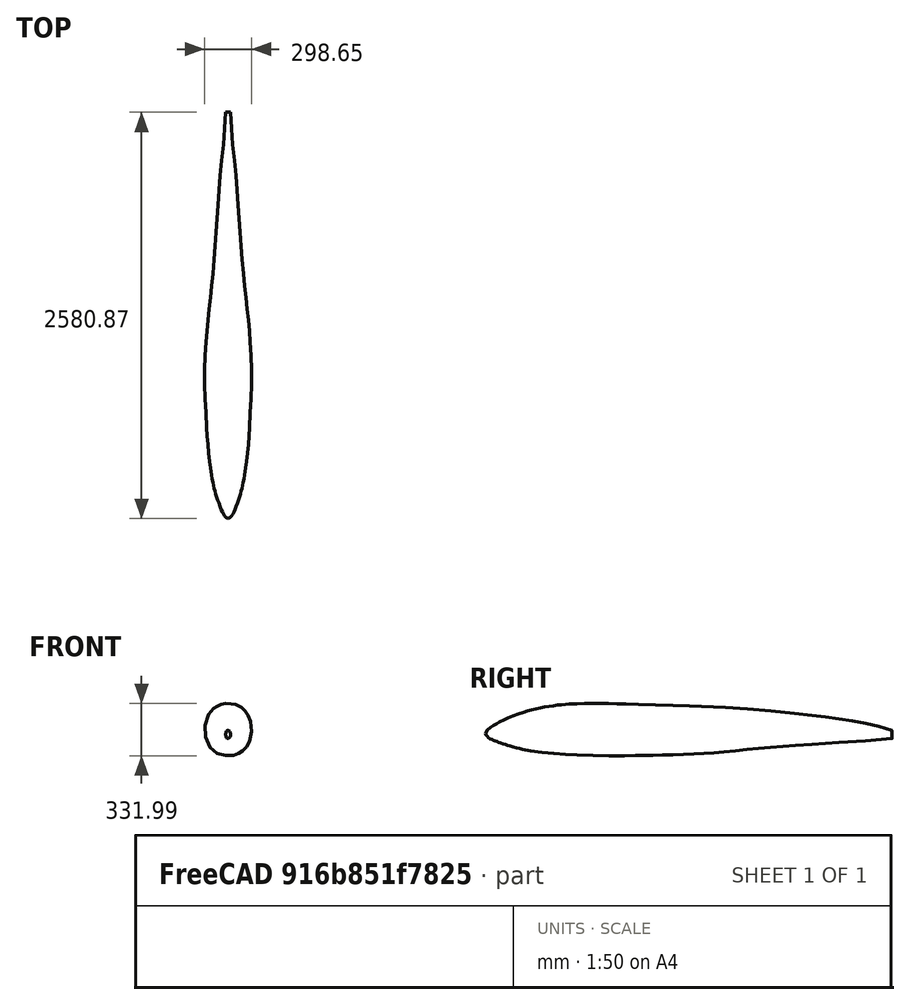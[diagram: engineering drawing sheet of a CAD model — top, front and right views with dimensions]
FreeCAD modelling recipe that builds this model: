
FCSTD DOCUMENT  (FreeCAD 1.0R39319 (Git))
Label: Drone body
License: All rights reserved
LicenseURL: https://en.wikipedia.org/wiki/All_rights_reserved
objects: Image::ImagePlane×3, Sketcher::SketchObject×3, Part::FeaturePython×2, PartDesign::Body×1
note: 9 computed .brp shape members not serialized (recipe doc carries the construction recipe); baked Part::Feature solids carry a one-line shape summary decoded from their .brp

FEATURE [PartDesign::Body] Body
  AllowCompound = false
  Origin = -> Origin
FEATURE [Image::ImagePlane] scheibe_sfh34_3v  label="Top"
  Placement = pos=(96.3,901.7,-4638.1) rot=(0,0,1;0rad)
  XSize = 5853.99
  YSize = 3489.71
FEATURE [Image::ImagePlane] scheibe_sfh34_3v001  label="Front"
  Placement = pos=(84.3,5726.3,1459.8) rot=(1,0,0;1.5708rad)
  XSize = 5853.99
  YSize = 3489.71
FEATURE [Image::ImagePlane] scheibe_sfh34_3v002  label="Right"
  Placement = pos=(-3758.7,-166.6,-638.5) rot=(0.57735,0.57735,0.57735;2.0944rad)
  XSize = 5853.99
  YSize = 3489.71
FEATURE [Sketcher::SketchObject] Sketch  label="HullCurve1"
  ArcFitTolerance = 1e-06
  FullyConstrained = false
  MakeInternals = false
  Placement = pos=(0,0,0) rot=(0.57735,0.57735,0.57735;2.0944rad)
  sketch-geometry (54):
    g0-g10: Circle [constr] x11 (B-spline internal-alignment scaffolding for g11; pole/knot coordinates omitted)
    g11: BSplineCurve PolesCount=11 KnotsCount=9 Degree=3 IsPeriodic=0
    g12-g20: GeomPoint [constr] x9 (B-spline internal-alignment scaffolding for g11; pole/knot coordinates omitted)
    g21-g34: Circle [constr] x14 (B-spline internal-alignment scaffolding for g35; pole/knot coordinates omitted)
    g35: BSplineCurve PolesCount=14 KnotsCount=12 Degree=3 IsPeriodic=0
    g36-g47: GeomPoint [constr] x12 (B-spline internal-alignment scaffolding for g35; pole/knot coordinates omitted)
    g48: Circle [constr] CenterX=2168.64 CenterY=101.192 CenterZ=0 NormalX=0 NormalY=0 NormalZ=1 AngleXU=0 Radius=1
    g49: Circle [constr] CenterX=2352.52 CenterY=83.7723 CenterZ=0 NormalX=0 NormalY=0 NormalZ=1 AngleXU=0 Radius=1
    g50: Circle [constr] CenterX=2583.1 CenterY=17.2095 CenterZ=0 NormalX=0 NormalY=0 NormalZ=1 AngleXU=0 Radius=1
    g51: BSplineCurve PolesCount=3 KnotsCount=2 Degree=2 IsPeriodic=0
    g52: GeomPoint [constr] X=2168.64 Y=101.192 Z=0
    g53: GeomPoint [constr] X=2583.1 Y=17.2095 Z=0
  constraints (22):
    c: Weight(g0) = 1
    c: Equal(g0, g1-g10) x10
    c: InternalAlignment(g0-g10 -> g11) x11
    c: InternalAlignment(g12-g20 -> g11) x9
    c: Coincident(g0,g-1)
    c: PointOnObject(g1,g-2)
    c: Weight(g21) = 1
    c: Equal(g21, g22-g34) x13
    c: InternalAlignment(g21-g34 -> g35) x14
    c: InternalAlignment(g36-g47 -> g35) x12
    c: Coincident(g21,g11)
    c: PointOnObject(g22,g-2)
    c: Weight(g48) = 1
    c: Equal(g48,g49)
    c: Equal(g48,g50)
    c: InternalAlignment(g48,g51)
    c: InternalAlignment(g49,g51)
    c: InternalAlignment(g50,g51)
    c: InternalAlignment(g52,g51)
    c: InternalAlignment(g53,g51)
    c: Coincident(g48,g11)
    c: Vertical(g35,g51)
FEATURE [Sketcher::SketchObject] Sketch001  label="HullCurve2"
  ArcFitTolerance = 1e-06
  FullyConstrained = false
  MakeInternals = false
  sketch-geometry (50):
    g0-g12: Circle [constr] x13 (B-spline internal-alignment scaffolding for g13; pole/knot coordinates omitted)
    g13: BSplineCurve PolesCount=13 KnotsCount=11 Degree=3 IsPeriodic=0
    g14-g24: GeomPoint [constr] x11 (B-spline internal-alignment scaffolding for g13; pole/knot coordinates omitted)
    g25: BSplineCurve PolesCount=13 KnotsCount=11 Degree=3 IsPeriodic=0
    g26-g38: Circle [constr] x13 (B-spline internal-alignment scaffolding for g25; pole/knot coordinates omitted)
    g39-g49: GeomPoint [constr] x11 (B-spline internal-alignment scaffolding for g25; pole/knot coordinates omitted)
  constraints (9):
    c: Weight(g0) = 1
    c: Equal(g0, g1-g12) x12
    c: InternalAlignment(g0-g12 -> g13) x13
    c: InternalAlignment(g14-g24 -> g13) x11
    c: Coincident(g0,g-1)
    c: PointOnObject(g1,g-1)
    c: Weight(g26) = 1
    c: Equal(g26, g27-g38) x12
    c: InternalAlignment(g26-g49 -> g25) x24
FEATURE [Sketcher::SketchObject] Sketch002  label="Profile"
  ArcFitTolerance = 1e-06
  FullyConstrained = true
  MakeInternals = false
  Placement = pos=(0,0,0) rot=(1,0,0;1.5708rad)
  sketch-geometry (10):
    g0-g3: Circle [constr] x4 (B-spline internal-alignment scaffolding for g4; pole/knot coordinates omitted)
    g4: BSplineCurve PolesCount=4 KnotsCount=5 Degree=3 IsPeriodic=1
    g5-g9: GeomPoint [constr] x5 (B-spline internal-alignment scaffolding for g4; pole/knot coordinates omitted)
  constraints (11):
    c: Weight(g0) = 1
    c: Equal(g0,g1)
    c: Equal(g0,g2)
    c: Equal(g0,g3)
    c: InternalAlignment(g0-g3 -> g4) x4
    c: InternalAlignment(g5-g9 -> g4) x5
    c: Symmetric(g0,g1,g-2)
    c: Symmetric(g3,g2,g-2)
    c: DistanceX(g0,g1) = 5
    c: DistanceY(g2,g1) = 5
    c: Symmetric(g2,g1,g-1)
FEATURE [Part::FeaturePython] CurvedArray  label="Body001"  # WARN: FeaturePython — macro-defined, semantics opaque (R4)
  Axis = (0,1,0)
  Base = -> Sketch002
  Distribution = 1
  DistributionReverse = false
  Hullcurves = -> [Sketch001,Sketch]
  Items = 20
  KeepBase = 0
  LoftMaxDegree = 2
  MaxLoftSize = 13
  OffsetEnd = 0
  OffsetStart = 0
  Solid = true
  Surface = false
  Twist = 0
FEATURE [Part::FeaturePython] wrib  # WARN: FeaturePython — macro-defined, semantics opaque (R4)
  Chord = 350
  Coordinates = (401) [(1.00008,0,0.00125721),(1.00002,0,0.00126996),(0.999839,0,0.00130819),(0.999534,0,0.00137188),(0.999106,0,0.00146099),(0.998557,0,0.00157543),+395 more]
  NacaNbrPoint = 200
  NacaProfil = 2412
  Placement = pos=(0,0,0) rot=(0.57735,0.57735,0.57735;2.0944rad)
  RibProfil = 2412
  Thickness = 0
  finite_TE = true
  splitSpline = true
  useSpline = true
  wingkey = 0
